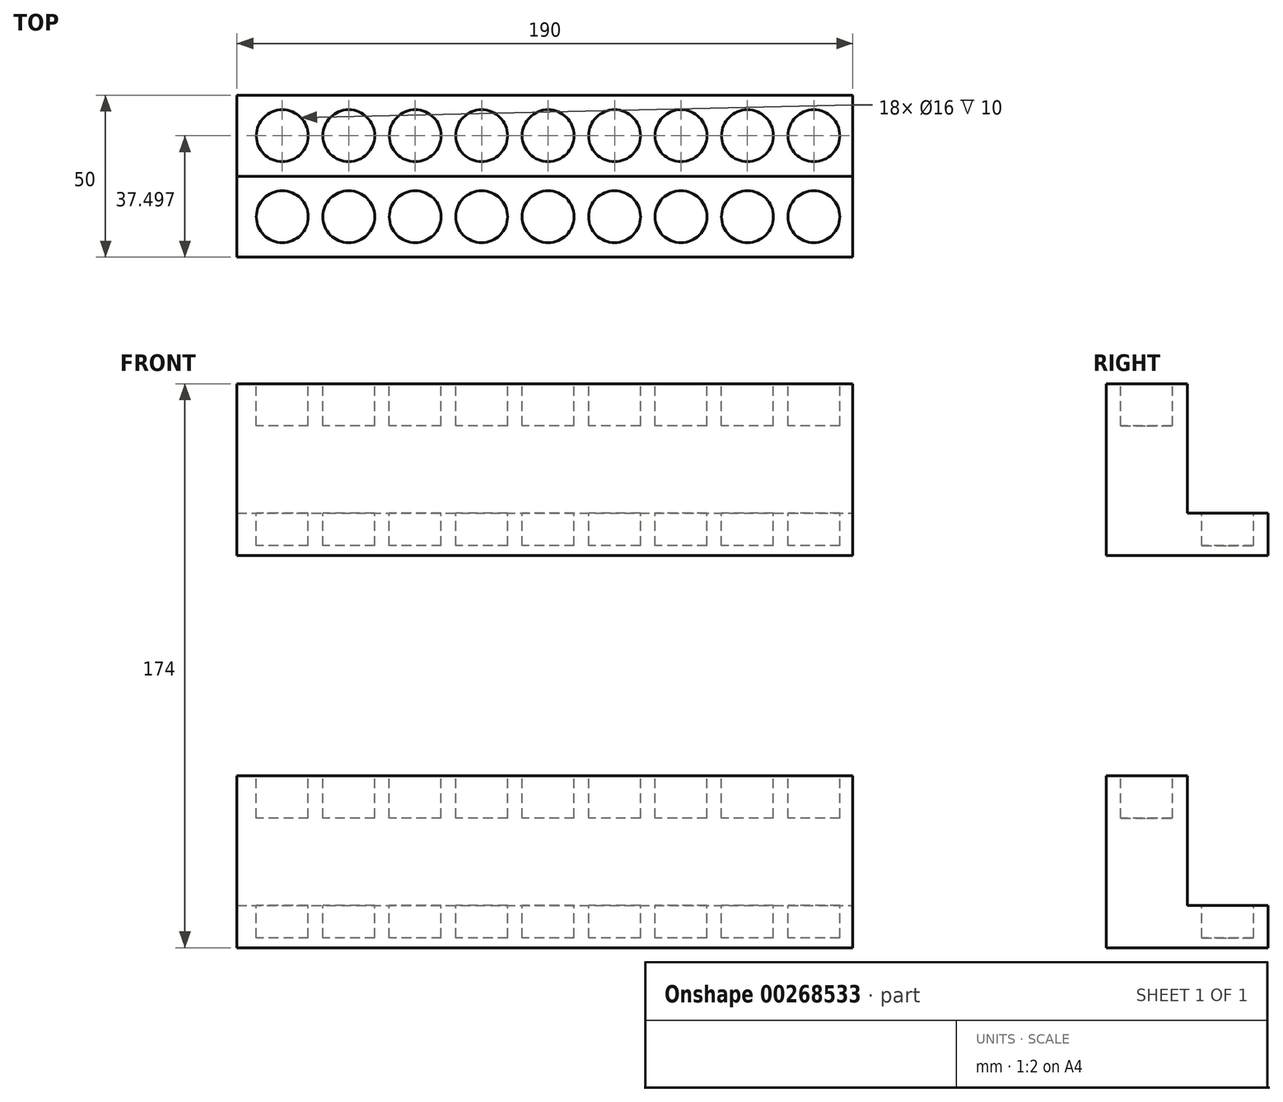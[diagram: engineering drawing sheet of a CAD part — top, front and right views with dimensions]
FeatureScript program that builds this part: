
annotation { "Feature Type Name" : "Feature", "Feature Type Description" : "" }
export const myFeature = defineFeature(function(context is Context, id is Id, definition is map)
    precondition{}
    {
        {
            var Q0;
            Q0=qCreatedBy(makeId("Top.planeOp"),FACE);
            var sketch = newSketch(context, id + "F0", { "sketchPlane" : qUnion([Q0])});
            skLineSegment(sketch, "E0.bottom", {"start": v(-117.92, 42.43) * mm, "end": v(72.08, 42.43) * mm});
            skLineSegment(sketch, "E0.top", {"start": v(-117.92, -7.57) * mm, "end": v(72.08, -7.57) * mm});
            skLineSegment(sketch, "E0.left", {"start": v(-117.92, 42.43) * mm, "end": v(-117.92, -7.57) * mm});
            skLineSegment(sketch, "E0.right", {"start": v(72.08, 42.43) * mm, "end": v(72.08, -7.57) * mm});
            skLineSegment(sketch, "E1", {"start": v(-117.92, 17.43) * mm, "end": v(72.08, 17.43) * mm});
            skCircle(sketch, "E2", {"center": v(-107.92, 29.93) * mm, "radius": 8 * mm});
            skCircle(sketch, "E3", {"center": v(-87.42, 29.93) * mm, "radius": 8 * mm});
            skCircle(sketch, "E4", {"center": v(-66.92, 29.93) * mm, "radius": 8 * mm});
            skCircle(sketch, "E5", {"center": v(-46.42, 29.93) * mm, "radius": 8 * mm});
            skCircle(sketch, "E6", {"center": v(-25.92, 29.93) * mm, "radius": 8 * mm});
            skCircle(sketch, "E7", {"center": v(-5.42, 29.93) * mm, "radius": 8 * mm});
            skCircle(sketch, "E8", {"center": v(15.08, 29.93) * mm, "radius": 8 * mm});
            skCircle(sketch, "E9", {"center": v(35.58, 29.93) * mm, "radius": 8 * mm});
            skCircle(sketch, "E10", {"center": v(56.08, 29.93) * mm, "radius": 8 * mm});
            skCircle(sketch, "E11", {"center": v(-107.92, 4.93) * mm, "radius": 8 * mm});
            skCircle(sketch, "E12", {"center": v(-87.42, 4.93) * mm, "radius": 8 * mm});
            skCircle(sketch, "E13", {"center": v(-66.92, 4.93) * mm, "radius": 8 * mm});
            skCircle(sketch, "E14", {"center": v(-46.42, 4.93) * mm, "radius": 8 * mm});
            skCircle(sketch, "E15", {"center": v(-25.92, 4.93) * mm, "radius": 8 * mm});
            skCircle(sketch, "E16", {"center": v(-5.42, 4.93) * mm, "radius": 8 * mm});
            skCircle(sketch, "E17", {"center": v(15.08, 4.93) * mm, "radius": 8 * mm});
            skCircle(sketch, "E18", {"center": v(35.58, 4.93) * mm, "radius": 8 * mm});
            skCircle(sketch, "E19", {"center": v(56.08, 4.93) * mm, "radius": 8 * mm});
            skLineSegment(sketch, "E20.bottom", {"start": v(-138.2, -85.5) * mm, "end": v(51.8, -85.5) * mm});
            skLineSegment(sketch, "E20.top", {"start": v(-138.2, -35.5) * mm, "end": v(51.8, -35.5) * mm});
            skLineSegment(sketch, "E20.left", {"start": v(-138.2, -85.5) * mm, "end": v(-138.2, -35.5) * mm});
            skLineSegment(sketch, "E20.right", {"start": v(51.8, -85.5) * mm, "end": v(51.8, -35.5) * mm});
            skLineSegment(sketch, "E21", {"start": v(-138.2, -60.5) * mm, "end": v(51.8, -60.5) * mm});
            skSolve(sketch);
        }
        {
            var Q0;
            {var subQ0=sQuery(id+"F0.wireOp",EDGE,"E20.top");Q0=makeQuery(id+"F0.imprint","IMPRINT",FACE,{"disambiguationData":[TD([[makeQuery(id+"F0.imprint","IMPRINT",EDGE,{"derivedFrom":subQ0}),-1.0]])]});}
            extrude(context, id + "F1", {"entities" : qUnion([Q0]), "depth" : 13 * mm});
        }
        {
            var Q0;
            {var subQ0=sQuery(id+"F0.wireOp",EDGE,"E20.bottom");Q0=makeQuery(id+"F0.imprint","IMPRINT",FACE,{"disambiguationData":[TD([[makeQuery(id+"F0.imprint","IMPRINT",EDGE,{"derivedFrom":subQ0}),1.0]])]});}
            extrude(context, id + "F2", {"entities" : qUnion([Q0]), "operationType" : NewBodyOperationType.ADD, "depth" : 53 * mm});
        }
        {
            var Q0;
            Q0=makeQuery(id+"F1.opExtrude","CAP_FACE",FACE,{"disambiguationData":[OSD([sQuery(id+"F0.wireOp",EDGE,"E20.top"),sQuery(id+"F0.wireOp",EDGE,"E20.left"),sQuery(id+"F0.wireOp",EDGE,"E20.right"),sQuery(id+"F0.wireOp",EDGE,"E21")])],"isStart":false});
            var sketch = newSketch(context, id + "F3", { "sketchPlane" : qUnion([Q0])});
            skCircle(sketch, "E22", {"center": v(-124.2, -48) * mm, "radius": 8 * mm});
            skCircle(sketch, "E23", {"center": v(-103.7, -48) * mm, "radius": 8 * mm});
            skCircle(sketch, "E24", {"center": v(-83.2, -48) * mm, "radius": 8 * mm});
            skCircle(sketch, "E25", {"center": v(-62.7, -48) * mm, "radius": 8 * mm});
            skCircle(sketch, "E26", {"center": v(-42.2, -48) * mm, "radius": 8 * mm});
            skCircle(sketch, "E27", {"center": v(-21.7, -48) * mm, "radius": 8 * mm});
            skCircle(sketch, "E28", {"center": v(-1.2, -48) * mm, "radius": 8 * mm});
            skCircle(sketch, "E29", {"center": v(19.3, -48) * mm, "radius": 8 * mm});
            skCircle(sketch, "E30", {"center": v(39.8, -48) * mm, "radius": 8 * mm});
            skSolve(sketch);
        }
        {
            var Q0;
            Q0=makeQuery(id+"F2.opExtrude","CAP_FACE",FACE,{"disambiguationData":[OSD([sQuery(id+"F0.wireOp",EDGE,"E20.bottom"),sQuery(id+"F0.wireOp",EDGE,"E20.left"),sQuery(id+"F0.wireOp",EDGE,"E20.right"),sQuery(id+"F0.wireOp",EDGE,"E21")])],"isStart":false});
            var sketch = newSketch(context, id + "F4", { "sketchPlane" : qUnion([Q0])});
            skCircle(sketch, "E31", {"center": v(-124.2, -73) * mm, "radius": 8 * mm});
            skCircle(sketch, "E32", {"center": v(-103.7, -73) * mm, "radius": 8 * mm});
            skCircle(sketch, "E33", {"center": v(-83.2, -73) * mm, "radius": 8 * mm});
            skCircle(sketch, "E34", {"center": v(-62.7, -73) * mm, "radius": 8 * mm});
            skCircle(sketch, "E35", {"center": v(-42.2, -73) * mm, "radius": 8 * mm});
            skCircle(sketch, "E36", {"center": v(-21.7, -73) * mm, "radius": 8 * mm});
            skCircle(sketch, "E37", {"center": v(-1.2, -73) * mm, "radius": 8 * mm});
            skCircle(sketch, "E38", {"center": v(19.3, -73) * mm, "radius": 8 * mm});
            skCircle(sketch, "E39", {"center": v(39.8, -73) * mm, "radius": 8 * mm});
            skSolve(sketch);
        }
        {
            var Q0;
            Q0=makeQuery(id+"F4.imprint","IMPRINT",FACE,{"disambiguationData":[TD([[makeQuery(id+"F4.imprint","IMPRINT",EDGE,{"derivedFrom":sQuery(id+"F4.wireOp",EDGE,"E39")}),1.0]])]});
            var Q1;
            Q1=makeQuery(id+"F4.imprint","IMPRINT",FACE,{"disambiguationData":[TD([[makeQuery(id+"F4.imprint","IMPRINT",EDGE,{"derivedFrom":sQuery(id+"F4.wireOp",EDGE,"E38")}),1.0]])]});
            var Q2;
            Q2=makeQuery(id+"F4.imprint","IMPRINT",FACE,{"disambiguationData":[TD([[makeQuery(id+"F4.imprint","IMPRINT",EDGE,{"derivedFrom":sQuery(id+"F4.wireOp",EDGE,"E37")}),1.0]])]});
            var Q3;
            Q3=makeQuery(id+"F4.imprint","IMPRINT",FACE,{"disambiguationData":[TD([[makeQuery(id+"F4.imprint","IMPRINT",EDGE,{"derivedFrom":sQuery(id+"F4.wireOp",EDGE,"E36")}),1.0]])]});
            var Q4;
            Q4=makeQuery(id+"F4.imprint","IMPRINT",FACE,{"disambiguationData":[TD([[makeQuery(id+"F4.imprint","IMPRINT",EDGE,{"derivedFrom":sQuery(id+"F4.wireOp",EDGE,"E35")}),1.0]])]});
            var Q5;
            Q5=makeQuery(id+"F4.imprint","IMPRINT",FACE,{"disambiguationData":[TD([[makeQuery(id+"F4.imprint","IMPRINT",EDGE,{"derivedFrom":sQuery(id+"F4.wireOp",EDGE,"E34")}),1.0]])]});
            var Q6;
            Q6=makeQuery(id+"F4.imprint","IMPRINT",FACE,{"disambiguationData":[TD([[makeQuery(id+"F4.imprint","IMPRINT",EDGE,{"derivedFrom":sQuery(id+"F4.wireOp",EDGE,"E33")}),1.0]])]});
            var Q7;
            Q7=makeQuery(id+"F4.imprint","IMPRINT",FACE,{"disambiguationData":[TD([[makeQuery(id+"F4.imprint","IMPRINT",EDGE,{"derivedFrom":sQuery(id+"F4.wireOp",EDGE,"E32")}),1.0]])]});
            var Q8;
            Q8=makeQuery(id+"F4.imprint","IMPRINT",FACE,{"disambiguationData":[TD([[makeQuery(id+"F4.imprint","IMPRINT",EDGE,{"derivedFrom":sQuery(id+"F4.wireOp",EDGE,"E31")}),1.0]])]});
            extrude(context, id + "F5", {"entities" : qUnion([Q0, Q1, Q2, Q3, Q4, Q5, Q6, Q7, Q8]), "operationType" : NewBodyOperationType.REMOVE, "oppositeDirection" : true, "depth" : 13 * mm});
        }
        {
            var Q0;
            Q0=makeQuery(id+"F3.imprint","IMPRINT",FACE,{"disambiguationData":[TD([[makeQuery(id+"F3.imprint","IMPRINT",EDGE,{"derivedFrom":sQuery(id+"F3.wireOp",EDGE,"E30")}),1.0]])]});
            var Q1;
            Q1=makeQuery(id+"F3.imprint","IMPRINT",FACE,{"disambiguationData":[TD([[makeQuery(id+"F3.imprint","IMPRINT",EDGE,{"derivedFrom":sQuery(id+"F3.wireOp",EDGE,"E29")}),1.0]])]});
            var Q2;
            Q2=makeQuery(id+"F3.imprint","IMPRINT",FACE,{"disambiguationData":[TD([[makeQuery(id+"F3.imprint","IMPRINT",EDGE,{"derivedFrom":sQuery(id+"F3.wireOp",EDGE,"E28")}),1.0]])]});
            var Q3;
            Q3=makeQuery(id+"F3.imprint","IMPRINT",FACE,{"disambiguationData":[TD([[makeQuery(id+"F3.imprint","IMPRINT",EDGE,{"derivedFrom":sQuery(id+"F3.wireOp",EDGE,"E27")}),1.0]])]});
            var Q4;
            Q4=makeQuery(id+"F3.imprint","IMPRINT",FACE,{"disambiguationData":[TD([[makeQuery(id+"F3.imprint","IMPRINT",EDGE,{"derivedFrom":sQuery(id+"F3.wireOp",EDGE,"E26")}),1.0]])]});
            var Q5;
            Q5=makeQuery(id+"F3.imprint","IMPRINT",FACE,{"disambiguationData":[TD([[makeQuery(id+"F3.imprint","IMPRINT",EDGE,{"derivedFrom":sQuery(id+"F3.wireOp",EDGE,"E25")}),1.0]])]});
            var Q6;
            Q6=makeQuery(id+"F3.imprint","IMPRINT",FACE,{"disambiguationData":[TD([[makeQuery(id+"F3.imprint","IMPRINT",EDGE,{"derivedFrom":sQuery(id+"F3.wireOp",EDGE,"E24")}),1.0]])]});
            var Q7;
            Q7=makeQuery(id+"F3.imprint","IMPRINT",FACE,{"disambiguationData":[TD([[makeQuery(id+"F3.imprint","IMPRINT",EDGE,{"derivedFrom":sQuery(id+"F3.wireOp",EDGE,"E23")}),1.0]])]});
            var Q8;
            Q8=makeQuery(id+"F3.imprint","IMPRINT",FACE,{"disambiguationData":[TD([[makeQuery(id+"F3.imprint","IMPRINT",EDGE,{"derivedFrom":sQuery(id+"F3.wireOp",EDGE,"E22")}),1.0]])]});
            extrude(context, id + "F6", {"entities" : qUnion([Q0, Q1, Q2, Q3, Q4, Q5, Q6, Q7, Q8]), "operationType" : NewBodyOperationType.REMOVE, "oppositeDirection" : true, "depth" : 10 * mm});
        }
        {
            var Q0;
            Q0=makeQuery(id+"F1.opExtrude","SWEPT_BODY",BODY,{"disambiguationData":[OSD([sQuery(id+"F0.wireOp",EDGE,"E20.top"),sQuery(id+"F0.wireOp",EDGE,"E20.left"),sQuery(id+"F0.wireOp",EDGE,"E20.right"),sQuery(id+"F0.wireOp",EDGE,"E21")])]});
            transform(context, id + "F7", {"entities" : qUnion([Q0]), "transformType" : TransformType.TRANSLATION_3D, "dx" : 0 * mm, "dy" : 0 * mm, "dz" : -121 * mm, "makeCopy" : true});
        }
    });
